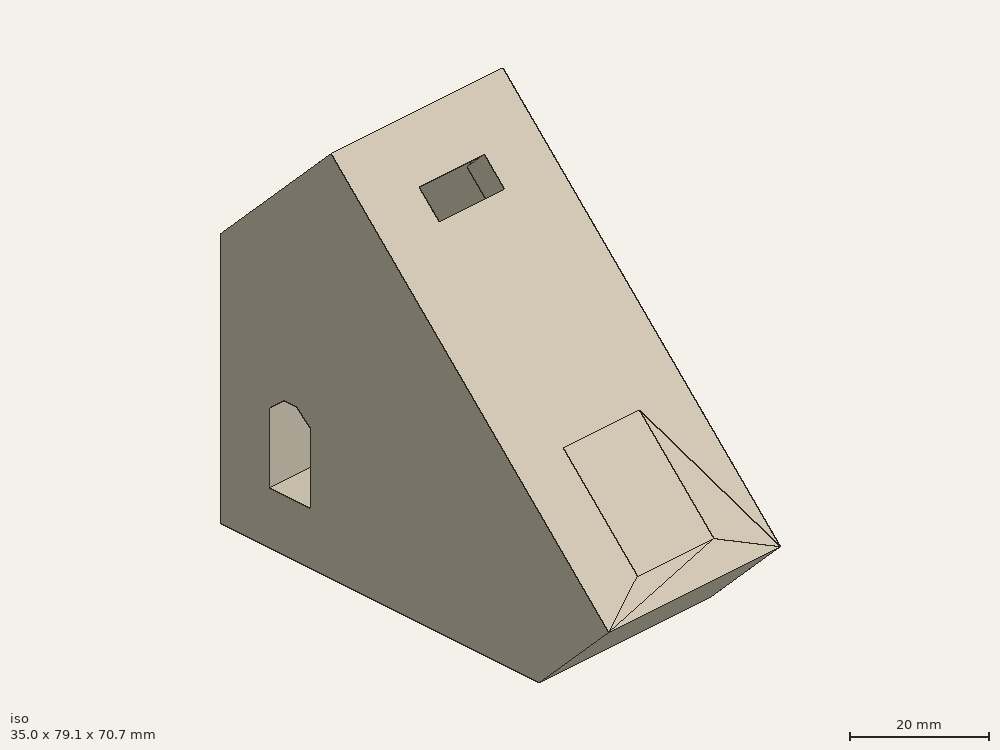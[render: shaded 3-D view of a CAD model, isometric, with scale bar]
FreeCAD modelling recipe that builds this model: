
FCSTD DOCUMENT  (FreeCAD 0.18R4 (GitTag))
Label: 06_USB-single_v1.1
License: All rights reserved
LicenseURL: http://en.wikipedia.org/wiki/All_rights_reserved
objects: Sketcher::SketchObject×3, PartDesign::Pocket×2, Part::Feature×1, PartDesign::FeatureBase×1, Spreadsheet::Sheet×1, PartDesign::Pad×1, PartDesign::Body×1, App::Part×1
note: 12 computed .brp shape members not serialized (recipe doc carries the construction recipe); baked Part::Feature solids carry a one-line shape summary decoded from their .brp

FEATURE [Part::Feature] _6_USB_single_v1001_solid001  label="_6_USB_single_v1001 (Solid)001"
  Placement = pos=(0,0,0) rot=(1,0,0;1.5708rad)
  shape: bbox 35 x 79.14 x 70.71 mm, 115 faces (baked)
FEATURE [PartDesign::FeatureBase] BaseFeature
  BaseFeature = -> _6_USB_single_v1001_solid001
FEATURE [Sketcher::SketchObject] Sketch
  ExternalGeometry = -> [BaseFeature]
  MapMode = 5
  Placement = pos=(0,0,0) rot=(1,0,0;1.5708rad)
  Support = -> [BaseFeature]
  expr: Constraints[11] = Spreadsheet.accesInfDistParroi
  expr: Constraints[10] = Spreadsheet.accesInfDistParroi
  expr: Constraints[9] = Spreadsheet.accesInfDistParroi
  expr: Constraints[8] = Spreadsheet.accesInfDistParroi
  sketch-geometry (4):
    g0: LineSegment StartX=2 StartY=63 StartZ=0 EndX=33 EndY=63 EndZ=0
    g1: LineSegment StartX=33 StartY=63 StartZ=0 EndX=33 EndY=2 EndZ=0
    g2: LineSegment StartX=33 StartY=2 StartZ=0 EndX=2 EndY=2 EndZ=0
    g3: LineSegment StartX=2 StartY=2 StartZ=0 EndX=2 EndY=63 EndZ=0
  constraints (12):
    c: Coincident(g0,g1)
    c: Coincident(g1,g2)
    c: Coincident(g2,g3)
    c: Coincident(g3,g0)
    c: Horizontal(g0)
    c: Horizontal(g2)
    c: Vertical(g1)
    c: Vertical(g3)
    c: DistanceX(g-3,g0) = 2
    c: DistanceX(g1,g-4) = 2
    c: DistanceY(g0,g-3) = 2
    c: DistanceY(g-4,g1) = 2
FEATURE [Spreadsheet::Sheet] Spreadsheet
  cells = A2=accesInfDistParroi; B2(accesInfDistParroi)=2; A3=bordPorte; B3(bordPorte)=2; A4=profondeurPorte; B4(profondeurPorte)=1.5
FEATURE [PartDesign::Pocket] Pocket
  BaseFeature = -> BaseFeature
  Length = 1.5
  Length2 = 100
  Profile = -> Sketch
  Type = 0
  expr: Length = Spreadsheet.profondeurPorte
FEATURE [Sketcher::SketchObject] Sketch001
  ExternalGeometry = -> [Pocket]
  MapMode = 5
  Placement = pos=(0,1.5,-3e-16) rot=(1,0,0;1.5708rad)
  Support = -> [Pocket]
  expr: Constraints[11] = Spreadsheet.bordPorte
  expr: Constraints[10] = Spreadsheet.bordPorte
  expr: Constraints[9] = Spreadsheet.bordPorte
  expr: Constraints[8] = Spreadsheet.bordPorte
  sketch-geometry (4):
    g0: LineSegment StartX=4 StartY=61 StartZ=0 EndX=31 EndY=61 EndZ=0
    g1: LineSegment StartX=31 StartY=61 StartZ=0 EndX=31 EndY=4 EndZ=0
    g2: LineSegment StartX=31 StartY=4 StartZ=0 EndX=4 EndY=4 EndZ=0
    g3: LineSegment StartX=4 StartY=4 StartZ=0 EndX=4 EndY=61 EndZ=0
  constraints (12):
    c: Coincident(g0,g1)
    c: Coincident(g1,g2)
    c: Coincident(g2,g3)
    c: Coincident(g3,g0)
    c: Horizontal(g0)
    c: Horizontal(g2)
    c: Vertical(g1)
    c: Vertical(g3)
    c: DistanceY(g0,g-4) = 2
    c: DistanceX(g-4,g0) = 2
    c: DistanceY(g-5,g1) = 2
    c: DistanceX(g1,g-5) = 2
FEATURE [PartDesign::Pocket] Pocket001
  BaseFeature = -> Pocket
  Length = 5
  Length2 = 100
  Profile = -> Sketch001
  Type = 0
FEATURE [Sketcher::SketchObject] Sketch002
  ExternalGeometry = -> [Pocket001]
  MapMode = 5
  Placement = pos=(-1.3e-15,46.6421,46.6421) rot=(-1,0,0;0.785398rad)
  Support = -> [Pocket001]
  sketch-geometry (4):
    g0: LineSegment StartX=9.725 StartY=-19.087 StartZ=0 EndX=25.2249 EndY=-19.087 EndZ=0
    g1: LineSegment StartX=25.2249 StartY=-19.087 StartZ=0 EndX=25.2249 EndY=-40.587 EndZ=0
    g2: LineSegment StartX=25.2249 StartY=-40.587 StartZ=0 EndX=9.725 EndY=-40.587 EndZ=0
    g3: LineSegment StartX=9.725 StartY=-40.587 StartZ=0 EndX=9.725 EndY=-19.087 EndZ=0
  constraints (10):
    c: Coincident(g0,g1)
    c: Coincident(g1,g2)
    c: Coincident(g2,g3)
    c: Coincident(g3,g0)
    c: Horizontal(g0)
    c: Horizontal(g2)
    c: Vertical(g1)
    c: Vertical(g3)
    c: Coincident(g0,g-6)
    c: Coincident(g1,g-5)
FEATURE [PartDesign::Pad] Pad
  BaseFeature = -> Pocket001
  Length = 10
  Length2 = 100
  Profile = -> Sketch002
  Reversed = true
  Type = 3
  UpToFace = -> Pocket001 [Face84]
FEATURE [PartDesign::Body] Body
  BaseFeature = -> _6_USB_single_v1001_solid001
  Group = -> [BaseFeature,Sketch,Pocket,Sketch001,Pocket001,Sketch002,Pad]
  Origin = -> Origin001
  Placement = pos=(0,0,0) rot=(1,0,0;1.5708rad)
  Tip = -> Pad
FEATURE [App::Part] Part
  Group = -> [Body]
  Origin = -> Origin
